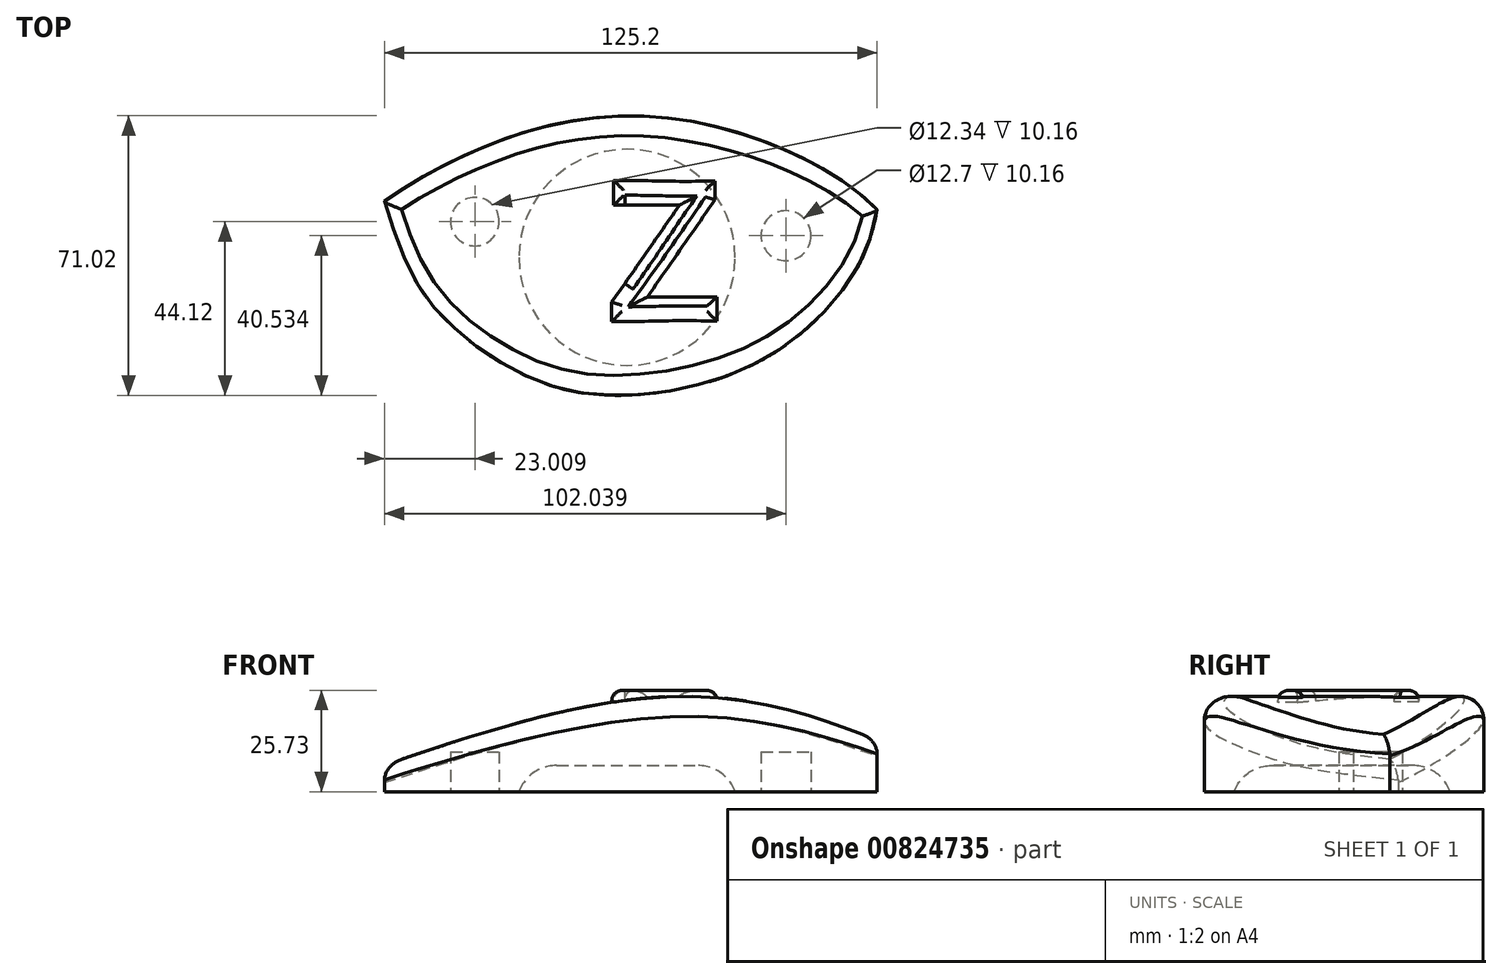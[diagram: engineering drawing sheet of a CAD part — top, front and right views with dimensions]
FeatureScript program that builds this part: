
annotation { "Feature Type Name" : "Feature", "Feature Type Description" : "" }
export const myFeature = defineFeature(function(context is Context, id is Id, definition is map)
    precondition{}
    {
        {
            var Q0;
            Q0=qCreatedBy(makeId("Top.planeOp"),FACE);
            var sketch = newSketch(context, id + "F0", { "sketchPlane" : qUnion([Q0])});
            skFitSpline(sketch, "E0", {"points": [v(-66.59, 5.22) * mm, v(0, 26.8) * mm, v(61.12, 0) * mm], "startDerivative": vector(99.52, 67.86) * mm, "endDerivative": vector(52.04, -74.12) * mm});
            skFitSpline(sketch, "E1", {"points": [v(61.12, 14.72) * mm, v(54.43, -9.94) * mm, v(30.28, -34.61) * mm, v(-7.75, -44.12) * mm, v(-33.19, -37.95) * mm, v(-56.31, -18.68) * mm, v(-66.59, 5.22) * mm], "startDerivative": vector(-51.02, -212.46) * mm, "endDerivative": vector(-50.72, 160.74) * mm});
            skSolve(sketch);
        }
        {
            var Q0;
            Q0=makeQuery(id+"F0.imprint","IMPRINT",FACE,{"disambiguationData":[TD([[makeQuery(id+"F0.imprint","IMPRINT",EDGE,{"derivedFrom":sQuery(id+"F0.wireOp",EDGE,"E0")}),-1.0]])]});
            extrude(context, id + "F1", {"entities" : qUnion([Q0]), "depth" : 43.18 * mm, "offsetDistance" : 25.4 * mm});
        }
        {
            var Q0;
            Q0=qCreatedBy(makeId("Front.planeOp"),FACE);
            var sketch = newSketch(context, id + "F2", { "sketchPlane" : qUnion([Q0])});
            skFitSpline(sketch, "E2", {"points": [v(-73.04, 13.07) * mm, v(13.7, 32.73) * mm, v(79.52, 12.3) * mm], "startDerivative": vector(169.08, 58.42) * mm, "endDerivative": vector(135.32, -62.5) * mm});
            skLineSegment(sketch, "E3", {"start": v(-73.04, 13.07) * mm, "end": v(-73.04, 55.43) * mm});
            skLineSegment(sketch, "E4", {"start": v(-73.04, 55.43) * mm, "end": v(73.97, 55.43) * mm});
            skLineSegment(sketch, "E5", {"start": v(73.97, 55.43) * mm, "end": v(79.52, 12.3) * mm});
            skSolve(sketch);
        }
        {
            var Q0;
            Q0 = qSketchRegion(id + "F2", true);
            extrude(context, id + "F3", {"entities" : qUnion([Q0]), "operationType" : NewBodyOperationType.REMOVE, "oppositeDirection" : true, "depth" : 381 * mm, "offsetDistance" : 25.4 * mm, "hasSecondDirection" : true, "secondDirectionOppositeDirection" : false, "secondDirectionDepth" : 254 * mm});
        }
        {
            var Q0;
            Q0=makeQuery(id+"F3.boolean.opBoolean","INTERSECT",EDGE,{"derivedFrom":[makeQuery(id+"F1.opExtrude","SWEPT_FACE",FACE,{"disambiguationData":[OSD([sQuery(id+"F0.wireOp",EDGE,"E1")])]}),makeQuery(id+"F3.opExtrude","SWEPT_FACE",FACE,{"disambiguationData":[OSD([sQuery(id+"F2.wireOp",EDGE,"E2")])]})]});
            var Q1;
            Q1=makeQuery(id+"F3.boolean.opBoolean","INTERSECT",EDGE,{"derivedFrom":[makeQuery(id+"F1.opExtrude","SWEPT_FACE",FACE,{"disambiguationData":[OSD([sQuery(id+"F0.wireOp",EDGE,"E0")])]}),makeQuery(id+"F3.opExtrude","SWEPT_FACE",FACE,{"disambiguationData":[OSD([sQuery(id+"F2.wireOp",EDGE,"E2")])]})]});
            fillet(context, id + "F4", {"entities" : qUnion([Q0, Q1]), "radius" : 5.08 * mm, "tangentPropagation" : true, "allowEdgeOverflow" : false});
        }
        {
            var Q0;
            Q0=makeQuery(id+"F1.opExtrude","CAP_FACE",FACE,{"disambiguationData":[OSD([sQuery(id+"F0.wireOp",EDGE,"E0"),sQuery(id+"F0.wireOp",EDGE,"E1")])],"isStart":true});
            var sketch = newSketch(context, id + "F5", { "sketchPlane" : qUnion([Q0])});
            skCircle(sketch, "E6", {"center": v(-4.93, 9.08) * mm, "radius": 28.08 * mm});
            skSolve(sketch);
        }
        {
            var Q0;
            Q0 = qSketchRegion(id + "F5", true);
            extrude(context, id + "F6", {"entities" : qUnion([Q0]), "operationType" : NewBodyOperationType.REMOVE, "oppositeDirection" : true, "depth" : 15.24 * mm, "offsetDistance" : 25.4 * mm});
        }
        {
            var Q0;
            Q0=makeQuery(id+"F6.boolean.opBoolean","COPY",EDGE,{"derivedFrom":makeQuery(id+"F6.opExtrude","CAP_EDGE",EDGE,{"disambiguationData":[OSD([sQuery(id+"F5.wireOp",EDGE,"E6")])],"isStart":false})});
            fillet(context, id + "F7", {"entities" : qUnion([Q0]), "radius" : 10.16 * mm, "tangentPropagation" : true, "allowEdgeOverflow" : false});
        }
        {
            var Q0;
            Q0=qCreatedBy(makeId("Top.planeOp"),FACE);
            cPlane(context, id + "F8", {"entities" : qUnion([Q0]), "cplaneType" : CPlaneType.OFFSET, "offset" : 34.3 * mm, "width" : 152.4 * mm, "height" : 152.4 * mm});
        }
        {
            var Q0;
            Q0=qCreatedBy(id+"F8.planeOp",FACE);
            var sketch = newSketch(context, id + "F9", { "sketchPlane" : qUnion([Q0])});
            skText(sketch, "E7", { "text": "Z", "fontName": "OpenSans-Bold.ttf"});
            const initialGuessF9  = {"E7": [-0.01002, -0.02539, 1, 0, 0.03616]};
            skSetInitialGuess(sketch, initialGuessF9);
            skSolve(sketch);
        }
        {
            var Q0;
            Q0=qCreatedBy(makeId("Front.planeOp"),FACE);
            var sketch = newSketch(context, id + "F10", { "sketchPlane" : qUnion([Q0])});
            skLineSegment(sketch, "E8.bottom", {"start": v(-71.83, -27.52) * mm, "end": v(77.08, -27.52) * mm});
            skLineSegment(sketch, "E8.top", {"start": v(-71.83, 8.56) * mm, "end": v(77.08, 8.56) * mm});
            skLineSegment(sketch, "E8.left", {"start": v(-71.83, -27.52) * mm, "end": v(-71.83, 8.56) * mm});
            skLineSegment(sketch, "E8.right", {"start": v(77.08, -27.52) * mm, "end": v(77.08, 8.56) * mm});
            skSolve(sketch);
        }
        {
            var Q0;
            Q0 = qSketchRegion(id + "F10", true);
            extrude(context, id + "F11", {"entities" : qUnion([Q0]), "operationType" : NewBodyOperationType.REMOVE, "depth" : 279.4 * mm, "offsetDistance" : 25.4 * mm, "hasSecondDirection" : true, "secondDirectionOppositeDirection" : true, "secondDirectionDepth" : 279.4 * mm});
        }
        {
            var Q0;
            Q0 = qSketchRegion(id + "F9", true);
            extrude(context, id + "F12", {"entities" : qUnion([Q0]), "operationType" : NewBodyOperationType.ADD, "endBound" : BoundingType.UP_TO_NEXT, "oppositeDirection" : true, "depth" : 25.4 * mm, "offsetDistance" : 25.4 * mm});
        }
        {
            var Q0;
            Q0=makeQuery(id+"F12.opExtrude","CAP_EDGE",EDGE,{"disambiguationData":[OSD([sQuery(id+"F9.wireOp",EDGE,"E7.sketch_text.stroke-3")])],"isStart":true});
            var Q1;
            Q1=makeQuery(id+"F12.opExtrude","CAP_EDGE",EDGE,{"disambiguationData":[OSD([sQuery(id+"F9.wireOp",EDGE,"E7.sketch_text.stroke-5")])],"isStart":true});
            var Q2;
            Q2=makeQuery(id+"F12.opExtrude","CAP_EDGE",EDGE,{"disambiguationData":[OSD([sQuery(id+"F9.wireOp",EDGE,"E7.sketch_text.stroke-6")])],"isStart":true});
            var Q3;
            Q3=makeQuery(id+"F12.opExtrude","CAP_EDGE",EDGE,{"disambiguationData":[OSD([sQuery(id+"F9.wireOp",EDGE,"E7.sketch_text.stroke-7")])],"isStart":true});
            var Q4;
            Q4=makeQuery(id+"F12.opExtrude","CAP_EDGE",EDGE,{"disambiguationData":[OSD([sQuery(id+"F9.wireOp",EDGE,"E7.sketch_text.stroke-8")])],"isStart":true});
            var Q5;
            Q5=makeQuery(id+"F12.opExtrude","CAP_EDGE",EDGE,{"disambiguationData":[OSD([sQuery(id+"F9.wireOp",EDGE,"E7.sketch_text.stroke-9")])],"isStart":true});
            var Q6;
            Q6=makeQuery(id+"F12.opExtrude","CAP_EDGE",EDGE,{"disambiguationData":[OSD([sQuery(id+"F9.wireOp",EDGE,"E7.sketch_text.stroke-0")])],"isStart":true});
            var Q7;
            Q7=makeQuery(id+"F12.opExtrude","CAP_EDGE",EDGE,{"disambiguationData":[OSD([sQuery(id+"F9.wireOp",EDGE,"E7.sketch_text.stroke-1")])],"isStart":true});
            var Q8;
            Q8=makeQuery(id+"F12.opExtrude","CAP_EDGE",EDGE,{"disambiguationData":[OSD([sQuery(id+"F9.wireOp",EDGE,"E7.sketch_text.stroke-2")])],"isStart":true});
            var Q9;
            Q9=makeQuery(id+"F12.opExtrude","CAP_EDGE",EDGE,{"disambiguationData":[OSD([sQuery(id+"F9.wireOp",EDGE,"E7.sketch_text.stroke-4")])],"isStart":true});
            fillet(context, id + "F13", {"entities" : qUnion([Q0, Q1, Q2, Q3, Q4, Q5, Q6, Q7, Q8, Q9]), "radius" : 2.54 * mm, "tangentPropagation" : true, "allowEdgeOverflow" : false});
        }
        {
            var Q0;
            Q0=makeQuery(id+"F11.boolean.opBoolean","COPY",FACE,{"derivedFrom":makeQuery(id+"F11.opExtrude","SWEPT_FACE",FACE,{"disambiguationData":[OSD([sQuery(id+"F10.wireOp",EDGE,"E8.top")])]})});
            var sketch = newSketch(context, id + "F14", { "sketchPlane" : qUnion([Q0])});
            skCircle(sketch, "E9", {"center": v(35.45, 3.59) * mm, "radius": 6.35 * mm});
            skCircle(sketch, "E10", {"center": v(-43.58, 0) * mm, "radius": 6.17 * mm});
            skSolve(sketch);
        }
        {
            var Q0;
            Q0=makeQuery(id+"F14.imprint","IMPRINT",FACE,{"disambiguationData":[TD([[makeQuery(id+"F14.imprint","IMPRINT",EDGE,{"derivedFrom":sQuery(id+"F14.wireOp",EDGE,"E9")}),1.0]])]});
            var Q1;
            Q1=makeQuery(id+"F14.imprint","IMPRINT",FACE,{"disambiguationData":[TD([[makeQuery(id+"F14.imprint","IMPRINT",EDGE,{"derivedFrom":sQuery(id+"F14.wireOp",EDGE,"E10")}),1.0]])]});
            extrude(context, id + "F15", {"entities" : qUnion([Q0, Q1]), "operationType" : NewBodyOperationType.REMOVE, "oppositeDirection" : true, "depth" : 10.16 * mm, "offsetDistance" : 25.4 * mm});
        }
    });
